# Revit family: Flag Range
name_source: partatom
category: Furniture
revit_build: Autodesk Revit 2018 (Build: 20170223_1515(x64)
units: mm (PartAtom-declared; Revit-internal decimal feet)

## family parameters
Always vertical = Yes
Cut with Voids When Loaded = No
OmniClass Number = 23.40.20.00
OmniClass Title = General Furniture and Specialties
Room Calculation Point = No
Shared = No
Work Plane-Based = No

## types (19) — shared parameters
Edge Material = Oak Veneered
Surface Material = Laminate (Sapphire Blue)

## per-type parameters (varying)
| type | Furniture Type |
| Dining Table (1500X700X740) | Flag Range Family : DiningTable 1500X700X740 |
| Dining Table (1800X700X740) | Flag Range Family : DiningTable 1800X700X740 |
| Dining Table (2000X700X740) | Flag Range Family : DiningTable 2000X700X740 |
| Dining Table (2400X700X740) | Flag Range Family : DiningTable 2400X700X740 |
| Dining Table (2700X700X740) | Flag Range Family : DiningTable 2700X700X740 |
| Dining Table (3000X700X740) | Flag Range Family : DiningTable 3000X700X740 |
| Dining Bench (1300X390X440X440) | Flag Range Family : DiningBench 1300X390X440 |
| Dining Bench (1600X390X440X440) | Flag Range Family : DiningBench 1600X390X440 |
| Dining Bench (1800X390X440X440) | Flag Range Family : DiningBench 1800X390X440 |
| Dining Bench (2200X390X440X440) | Flag Range Family : DiningBench 2200X390X440 |
| Dining Bench (2500X390X440X440) | Flag Range Family : DiningBench 2500X390X440 |
| Dining Bench (2800X390X440X440) | Flag Range Family : DiningBench 2800X390X440 |
| Bar Table (1500X700X1500) | Flag Range Family : BarTable 1500X700X1500 |
| Bar Table (1800X700X1500) | Flag Range Family : BarTable 1800X700X1500 |
| Bar Table (2000X700X1500) | Flag Range Family : BarTable 2000X700X1500 |
| Bar Table (2400X700X1500) | Flag Range Family : BarTable 2400X700X1500 |
| Bar Table (2700X700X1500) | Flag Range Family : BarTable 2700X700X1500 |
| Bar Table (3000X700X1500) | Flag Range Family : BarTable 3000X700X1500 |
| Bar Bench (950X390X780X780) | Flag Range Family : BarBench 950X390X780 |

## geometry (parser evidence)
native form markers: Sweep x6
no freeform markers — native parametric forms only
